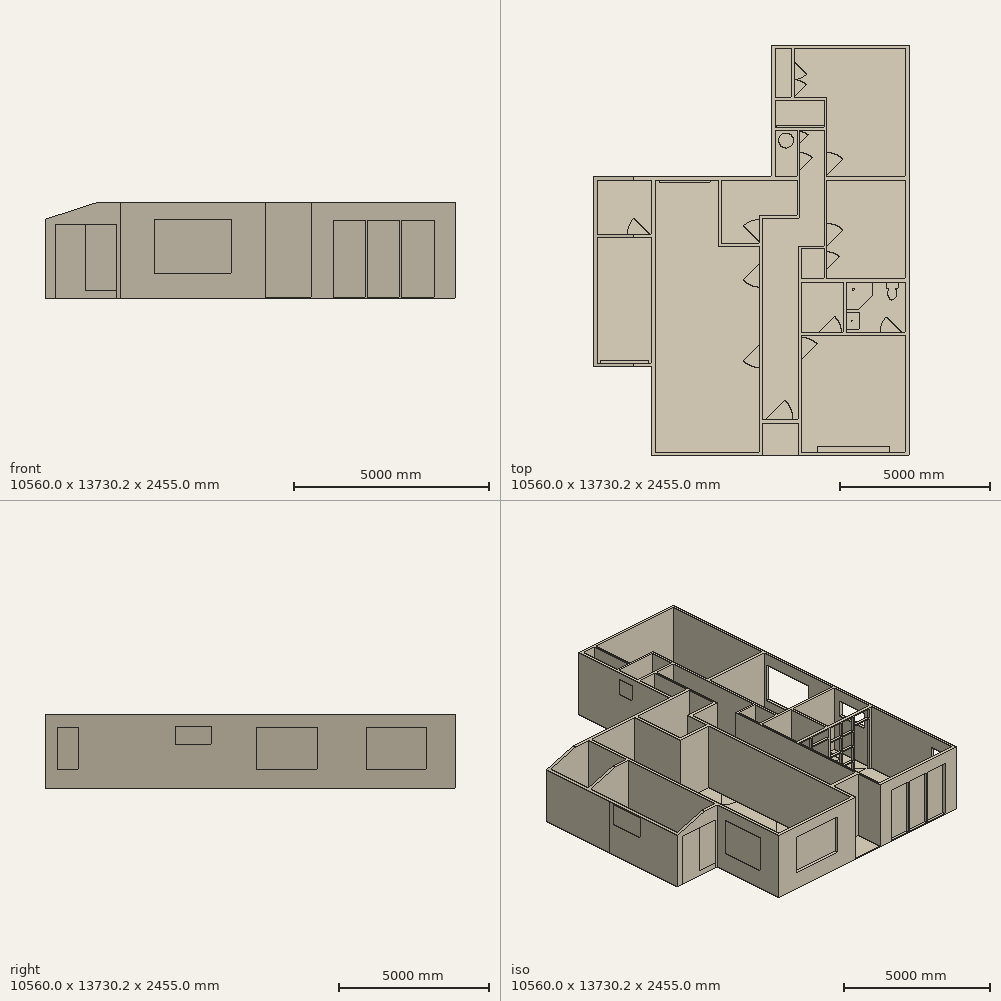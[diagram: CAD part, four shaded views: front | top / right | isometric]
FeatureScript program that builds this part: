
annotation { "Feature Type Name" : "Feature", "Feature Type Description" : "" }
export const myFeature = defineFeature(function(context is Context, id is Id, definition is map)
    precondition{}
    {
        {
            var Q0;
            Q0=qCreatedBy(makeId("Top.planeOp"),FACE);
            var sketch = newSketch(context, id + "F0", { "sketchPlane" : qUnion([Q0])});
            skLineSegment(sketch, "E0.bottom", {"start": v(0, 0) * mm, "end": v(3730, 0) * mm});
            skLineSegment(sketch, "E0.left", {"start": v(0, 0) * mm, "end": v(0, 2970) * mm});
            skLineSegment(sketch, "E0.right", {"start": v(3730, 0) * mm, "end": v(3730, 1060) * mm});
            skLineSegment(sketch, "E1.bottom", {"start": v(115, 115) * mm, "end": v(3615, 115) * mm});
            skLineSegment(sketch, "E2.bottom", {"start": v(3730, 1060) * mm, "end": v(4920, 1060) * mm});
            skLineSegment(sketch, "E2.right", {"start": v(4920, 1210) * mm, "end": v(4920, 7010) * mm});
            skLineSegment(sketch, "E3", {"start": v(3730, 1210) * mm, "end": v(4920, 1210) * mm});
            skLineSegment(sketch, "E4.bottom", {"start": v(5010, 5920) * mm, "end": v(5780, 5920) * mm});
            skLineSegment(sketch, "E4.top", {"start": v(4920, 0) * mm, "end": v(8625, 0) * mm});
            skLineSegment(sketch, "E4.left", {"start": v(4920, 5920) * mm, "end": v(4920, 1210) * mm});
            skLineSegment(sketch, "E4.right", {"start": v(8625, 5920) * mm, "end": v(8625, 0) * mm});
            skLineSegment(sketch, "E5.bottom", {"start": v(8510, 115) * mm, "end": v(5010, 115) * mm});
            skLineSegment(sketch, "E5.top", {"start": v(8510, 5805) * mm, "end": v(6510, 5805) * mm});
            skLineSegment(sketch, "E5.left", {"start": v(8510, 115) * mm, "end": v(8510, 4105) * mm});
            skLineSegment(sketch, "E5.right", {"start": v(5010, 115) * mm, "end": v(5010, 4105) * mm});
            skLineSegment(sketch, "E6", {"start": v(5780, 5920) * mm, "end": v(5780, 6920) * mm});
            skLineSegment(sketch, "E7", {"start": v(8625, 5920) * mm, "end": v(8625, 9335) * mm});
            skLineSegment(sketch, "E8", {"start": v(8510, 9335) * mm, "end": v(5870, 9335) * mm});
            skLineSegment(sketch, "E9.top", {"start": v(5870, 9220) * mm, "end": v(8510, 9220) * mm});
            skLineSegment(sketch, "E9.left", {"start": v(5870, 5920) * mm, "end": v(5870, 9220) * mm});
            skLineSegment(sketch, "E9.right", {"start": v(8510, 5920) * mm, "end": v(8510, 9220) * mm});
            skLineSegment(sketch, "E10.trimOffspring", {"start": v(5870, 5920) * mm, "end": v(8510, 5920) * mm});
            skLineSegment(sketch, "E11", {"start": v(5780, 7010) * mm, "end": v(4920, 7010) * mm});
            skLineSegment(sketch, "E12", {"start": v(5010, 5920) * mm, "end": v(5010, 6920) * mm});
            skLineSegment(sketch, "E13", {"start": v(5010, 6920) * mm, "end": v(5780, 6920) * mm});
            skLineSegment(sketch, "E14", {"start": v(3615, 7000) * mm, "end": v(2235, 7000) * mm});
            skLineSegment(sketch, "E15", {"start": v(2235, 7000) * mm, "end": v(2235, 9220) * mm});
            skLineSegment(sketch, "E16", {"start": v(2235, 9335) * mm, "end": v(4025, 9335) * mm});
            skLineSegment(sketch, "E17", {"start": v(4025, 9335) * mm, "end": v(4025, 13730) * mm});
            skLineSegment(sketch, "E18", {"start": v(4025, 13730) * mm, "end": v(8625, 13730) * mm});
            skLineSegment(sketch, "E19", {"start": v(8625, 9335) * mm, "end": v(8625, 13730) * mm});
            skLineSegment(sketch, "E20", {"start": v(5780, 9335) * mm, "end": v(5780, 10895) * mm});
            skLineSegment(sketch, "E21", {"start": v(5780, 11895) * mm, "end": v(4140, 11895) * mm});
            skLineSegment(sketch, "E22", {"start": v(5870, 9335) * mm, "end": v(5870, 11985) * mm});
            skLineSegment(sketch, "E23", {"start": v(5870, 11985) * mm, "end": v(4770, 11985) * mm});
            skLineSegment(sketch, "E24", {"start": v(4140, 11985) * mm, "end": v(4140, 13615) * mm});
            skLineSegment(sketch, "E25", {"start": v(4140, 13615) * mm, "end": v(4680, 13615) * mm});
            skLineSegment(sketch, "E26", {"start": v(8510, 13615) * mm, "end": v(8510, 9335) * mm});
            skLineSegment(sketch, "E27", {"start": v(4140, 9335) * mm, "end": v(4870, 9335) * mm});
            skLineSegment(sketch, "E28", {"start": v(3615, 7115) * mm, "end": v(2350, 7115) * mm});
            skLineSegment(sketch, "E29", {"start": v(2350, 7115) * mm, "end": v(2350, 9220) * mm});
            skLineSegment(sketch, "E30", {"start": v(2350, 9220) * mm, "end": v(4870, 9220) * mm});
            skLineSegment(sketch, "E31", {"start": v(4870, 9220) * mm, "end": v(4870, 8040) * mm});
            skLineSegment(sketch, "E32", {"start": v(4870, 8040) * mm, "end": v(3615, 8040) * mm});
            skLineSegment(sketch, "E33", {"start": v(4960, 7925) * mm, "end": v(4960, 9335) * mm});
            skLineSegment(sketch, "E34", {"start": v(4140, 11895) * mm, "end": v(4140, 10985) * mm});
            skLineSegment(sketch, "E35", {"start": v(4140, 10895) * mm, "end": v(5780, 10895) * mm});
            skLineSegment(sketch, "E36.trimOffspring", {"start": v(4140, 10895) * mm, "end": v(4140, 9335) * mm});
            skLineSegment(sketch, "E37.trimOffspring", {"start": v(5780, 10985) * mm, "end": v(5780, 11895) * mm});
            skLineSegment(sketch, "E38", {"start": v(4770, 13615) * mm, "end": v(4770, 11985) * mm});
            skLineSegment(sketch, "E39", {"start": v(4680, 13615) * mm, "end": v(4680, 11985) * mm});
            skLineSegment(sketch, "E40.trimOffspring", {"start": v(4770, 13615) * mm, "end": v(8510, 13615) * mm});
            skLineSegment(sketch, "E41.trimOffspring", {"start": v(4680, 11985) * mm, "end": v(4140, 11985) * mm});
            skLineSegment(sketch, "E42", {"start": v(2235, 9335) * mm, "end": v(-1935, 9335) * mm});
            skLineSegment(sketch, "E43", {"start": v(-1935, 9335) * mm, "end": v(-1935, 7285) * mm});
            skLineSegment(sketch, "E44", {"start": v(-1820, 7285) * mm, "end": v(0, 7285) * mm});
            skLineSegment(sketch, "E45", {"start": v(0, 9220) * mm, "end": v(-1820, 9220) * mm});
            skLineSegment(sketch, "E46", {"start": v(-1820, 9220) * mm, "end": v(-1820, 7400) * mm});
            skLineSegment(sketch, "E47", {"start": v(-1820, 7400) * mm, "end": v(0, 7400) * mm});
            skLineSegment(sketch, "E48", {"start": v(0, 9220) * mm, "end": v(0, 7400) * mm});
            skLineSegment(sketch, "E49", {"start": v(115, 9220) * mm, "end": v(2235, 9220) * mm});
            skLineSegment(sketch, "E50", {"start": v(4960, 9335) * mm, "end": v(4960, 10895) * mm});
            skLineSegment(sketch, "E51", {"start": v(4870, 10895) * mm, "end": v(4870, 9335) * mm});
            skLineSegment(sketch, "E52", {"start": v(115, 9220) * mm, "end": v(115, 115) * mm});
            skLineSegment(sketch, "E53", {"start": v(-1935, 7285) * mm, "end": v(-1935, 2970) * mm});
            skLineSegment(sketch, "E54", {"start": v(-1935, 2970) * mm, "end": v(0, 2970) * mm});
            skLineSegment(sketch, "E55", {"start": v(-1820, 7285) * mm, "end": v(-1820, 3085) * mm});
            skLineSegment(sketch, "E56", {"start": v(-1820, 3085) * mm, "end": v(0, 3085) * mm});
            skPoint(sketch, "E57", {"position": v(4960, 10895) * mm});
            skLineSegment(sketch, "E58", {"start": v(4140, 10985) * mm, "end": v(5780, 10985) * mm});
            skLineSegment(sketch, "E59", {"start": v(3615, 7115) * mm, "end": v(3615, 8040) * mm});
            skLineSegment(sketch, "E60.trimOffspring", {"start": v(0, 7285) * mm, "end": v(0, 3085) * mm});
            skLineSegment(sketch, "E61.trimOffspring", {"start": v(3730, 7925) * mm, "end": v(4960, 7925) * mm});
            skLineSegment(sketch, "E62.trimOffspring", {"start": v(4920, 1060) * mm, "end": v(4920, 0) * mm});
            skLineSegment(sketch, "E63.trimOffspring", {"start": v(5780, 7010) * mm, "end": v(5780, 9335) * mm});
            skLineSegment(sketch, "E64", {"start": v(6510, 4105) * mm, "end": v(6510, 5805) * mm});
            skLineSegment(sketch, "E65", {"start": v(6410, 4105) * mm, "end": v(6410, 5805) * mm});
            skLineSegment(sketch, "E66", {"start": v(3730, 7925) * mm, "end": v(3730, 1210) * mm});
            skLineSegment(sketch, "E67", {"start": v(3615, 7000) * mm, "end": v(3615, 115) * mm});
            skLineSegment(sketch, "E68.trimOffspring", {"start": v(6410, 5805) * mm, "end": v(5010, 5805) * mm});
            skLineSegment(sketch, "E69.trimOffspring", {"start": v(8510, 4105) * mm, "end": v(8510, 5805) * mm});
            skLineSegment(sketch, "E70.trimOffspring", {"start": v(5010, 4105) * mm, "end": v(5010, 5805) * mm});
            skLineSegment(sketch, "E71", {"start": v(6410, 4105) * mm, "end": v(6510, 4105) * mm});
            skSolve(sketch);
        }
        {
            var Q0;
            Q0=makeQuery(id+"F0.imprint","IMPRINT",FACE,{"disambiguationData":[TD([[makeQuery(id+"F0.imprint","IMPRINT",EDGE,{"derivedFrom":sQuery(id+"F0.wireOp",EDGE,"E0.bottom")}),1.0]])]});
            var Q1;
            {var subQ0=sQuery(id+"F0.wireOp",EDGE,"E2.bottom");Q1=makeQuery(id+"F0.imprint","IMPRINT",FACE,{"disambiguationData":[TD([[makeQuery(id+"F0.imprint","IMPRINT",EDGE,{"derivedFrom":subQ0}),1.0]])]});}
            var Q2;
            {var subQ3=sQuery(id+"F0.wireOp",EDGE,"E4.bottom");Q2=makeQuery(id+"F0.imprint","IMPRINT",FACE,{"disambiguationData":[TD([[makeQuery(id+"F0.imprint","IMPRINT",EDGE,{"derivedFrom":subQ3}),-1.0]])]});}
            extrude(context, id + "F1", {"entities" : qUnion([Q0, Q1, Q2]), "depth" : 2430 * mm});
        }
        {
            var Q0;
            Q0=qCreatedBy(makeId("Front.planeOp"),FACE);
            var sketch = newSketch(context, id + "F2", { "sketchPlane" : qUnion([Q0])});
            skLineSegment(sketch, "E72", {"start": v(0, 0) * mm, "end": v(0, 2430) * mm});
            skLineSegment(sketch, "E73", {"start": v(0, 2430) * mm, "end": v(-1935, 1850) * mm, "construction": true});
            skLineSegment(sketch, "E74", {"start": v(-1935, 1850) * mm, "end": v(-1935, 3117.7) * mm});
            skLineSegment(sketch, "E75", {"start": v(-1935, 3117.7) * mm, "end": v(0, 3117.7) * mm});
            skLineSegment(sketch, "E76", {"start": v(0, 3117.7) * mm, "end": v(0, 2430) * mm});
            skLineSegment(sketch, "E77", {"start": v(-1935, 2005) * mm, "end": v(0, 2630) * mm});
            skSolve(sketch);
        }
        {
            var Q0;
            Q0=qSketchRegion(id+"F2",true);
            extrude(context, id + "F3", {"entities" : qUnion([Q0]), "operationType" : NewBodyOperationType.REMOVE, "endBound" : BoundingType.THROUGH_ALL, "oppositeDirection" : true, "depth" : 25 * mm});
        }
        {
            var Q0;
            Q0=qCreatedBy(makeId("Top.planeOp"),FACE);
            var sketch = newSketch(context, id + "F4", { "sketchPlane" : qUnion([Q0])});
            skLineSegment(sketch, "E78", {"start": v(0, 0) * mm, "end": v(8625, 0) * mm});
            skLineSegment(sketch, "E79", {"start": v(8625, 0) * mm, "end": v(8625, 13730) * mm});
            skLineSegment(sketch, "E80", {"start": v(8625, 13730) * mm, "end": v(4025, 13730) * mm});
            skLineSegment(sketch, "E81", {"start": v(4025, 13730) * mm, "end": v(4025, 9335) * mm});
            skLineSegment(sketch, "E82", {"start": v(4025, 9335) * mm, "end": v(-1935, 9335) * mm});
            skLineSegment(sketch, "E83", {"start": v(-1935, 9335) * mm, "end": v(-1935, 2970) * mm});
            skLineSegment(sketch, "E84", {"start": v(-1935, 2970) * mm, "end": v(0, 2970) * mm});
            skLineSegment(sketch, "E85", {"start": v(0, 2970) * mm, "end": v(0, 0) * mm});
            skSolve(sketch);
        }
        {
            var Q0;
            Q0=qSketchRegion(id+"F4",true);
            extrude(context, id + "F5", {"entities" : qUnion([Q0]), "operationType" : NewBodyOperationType.ADD, "oppositeDirection" : true, "depth" : 25 * mm});
        }
        {
            var Q0;
            Q0=makeQuery(id+"F1.opExtrude","SWEPT_FACE",FACE,{"disambiguationData":[OSD([sQuery(id+"F0.wireOp",EDGE,"E71")])]});
            var sketch = newSketch(context, id + "F6", { "sketchPlane" : qUnion([Q0])});
            skLineSegment(sketch, "E86", {"start": v(6410, 0) * mm, "end": v(6410, 1980) * mm});
            skLineSegment(sketch, "E87", {"start": v(6410, 2430) * mm, "end": v(6510, 2430) * mm});
            skLineSegment(sketch, "E88", {"start": v(6510, 2385) * mm, "end": v(6510, 1833.75) * mm});
            skLineSegment(sketch, "E89", {"start": v(6510, 0) * mm, "end": v(6410, 0) * mm});
            skLineSegment(sketch, "E90", {"start": v(6410, 2430) * mm, "end": v(5010, 2430) * mm});
            skLineSegment(sketch, "E91", {"start": v(5010, 2430) * mm, "end": v(5010, 0) * mm});
            skLineSegment(sketch, "E92", {"start": v(5010, 0) * mm, "end": v(5650, 0) * mm});
            skLineSegment(sketch, "E93", {"start": v(6510, 2430) * mm, "end": v(8510, 2430) * mm});
            skLineSegment(sketch, "E94", {"start": v(8510, 2430) * mm, "end": v(8510, 0) * mm});
            skLineSegment(sketch, "E95", {"start": v(8510, 0) * mm, "end": v(8420, 0) * mm});
            skLineSegment(sketch, "E96", {"start": v(5055, 45) * mm, "end": v(5055, 596.25) * mm});
            skLineSegment(sketch, "E97", {"start": v(5055, 2385) * mm, "end": v(5605, 2385) * mm});
            skLineSegment(sketch, "E98", {"start": v(5055, 45) * mm, "end": v(5605, 45) * mm});
            skLineSegment(sketch, "E99", {"start": v(5605, 45) * mm, "end": v(5605, 596.25) * mm});
            skLineSegment(sketch, "E100", {"start": v(5650, 0) * mm, "end": v(5650, 1980) * mm});
            skLineSegment(sketch, "E101", {"start": v(5650, 1980) * mm, "end": v(6410, 1980) * mm});
            skLineSegment(sketch, "E102", {"start": v(6410, 1980) * mm, "end": v(6410, 0) * mm});
            skLineSegment(sketch, "E103", {"start": v(5650, 2025) * mm, "end": v(5650, 2385) * mm});
            skLineSegment(sketch, "E104", {"start": v(5650, 2025) * mm, "end": v(6410, 2025) * mm});
            skLineSegment(sketch, "E105", {"start": v(7660, 0) * mm, "end": v(7660, 1980) * mm});
            skLineSegment(sketch, "E106", {"start": v(7660, 1980) * mm, "end": v(8420, 1980) * mm});
            skLineSegment(sketch, "E107", {"start": v(8420, 1980) * mm, "end": v(8420, 0) * mm});
            skLineSegment(sketch, "E108", {"start": v(6510, 2385) * mm, "end": v(7062.5, 2385) * mm});
            skLineSegment(sketch, "E109", {"start": v(8420, 2025) * mm, "end": v(7660, 2025) * mm});
            skLineSegment(sketch, "E110", {"start": v(7615, 2025) * mm, "end": v(7615, 1833.75) * mm});
            skLineSegment(sketch, "E111", {"start": v(8420, 2385) * mm, "end": v(8420, 2025) * mm});
            skLineSegment(sketch, "E112", {"start": v(7615, 2025) * mm, "end": v(7615, 2385) * mm});
            skLineSegment(sketch, "E113", {"start": v(7660, 2025) * mm, "end": v(7660, 2385) * mm});
            skLineSegment(sketch, "E114", {"start": v(6510, 45) * mm, "end": v(7062.5, 45) * mm});
            skLineSegment(sketch, "E115", {"start": v(6510, 596.25) * mm, "end": v(7062.5, 596.25) * mm});
            skLineSegment(sketch, "E116", {"start": v(6510, 641.25) * mm, "end": v(7062.5, 641.25) * mm});
            skLineSegment(sketch, "E117", {"start": v(7615, 1192.5) * mm, "end": v(7107.5, 1192.5) * mm});
            skLineSegment(sketch, "E118", {"start": v(6510, 1237.5) * mm, "end": v(7062.5, 1237.5) * mm});
            skLineSegment(sketch, "E119", {"start": v(6510, 1788.75) * mm, "end": v(7062.5, 1788.75) * mm});
            skLineSegment(sketch, "E120", {"start": v(6510, 1833.75) * mm, "end": v(7062.5, 1833.75) * mm});
            skLineSegment(sketch, "E121", {"start": v(5605, 596.25) * mm, "end": v(5055, 596.25) * mm});
            skLineSegment(sketch, "E122", {"start": v(5055, 641.25) * mm, "end": v(5605, 641.25) * mm});
            skLineSegment(sketch, "E123", {"start": v(5605, 1192.5) * mm, "end": v(5055, 1192.5) * mm});
            skLineSegment(sketch, "E124", {"start": v(5055, 1237.5) * mm, "end": v(5605, 1237.5) * mm});
            skLineSegment(sketch, "E125", {"start": v(5605, 1788.75) * mm, "end": v(5055, 1788.75) * mm});
            skLineSegment(sketch, "E126", {"start": v(5055, 1833.75) * mm, "end": v(5605, 1833.75) * mm});
            skLineSegment(sketch, "E127", {"start": v(5207.26, 2385) * mm, "end": v(5207.26, 1833.75) * mm, "construction": true});
            skLineSegment(sketch, "E128", {"start": v(5202.38, 1788.75) * mm, "end": v(5202.38, 1237.5) * mm, "construction": true});
            skLineSegment(sketch, "E129", {"start": v(5202.38, 1192.5) * mm, "end": v(5202.38, 641.25) * mm, "construction": true});
            skLineSegment(sketch, "E130", {"start": v(5196.62, 596.25) * mm, "end": v(5196.62, 45) * mm, "construction": true});
            skLineSegment(sketch, "E131", {"start": v(6622.85, 45) * mm, "end": v(6622.85, 596.25) * mm, "construction": true});
            skLineSegment(sketch, "E132", {"start": v(6622.85, 641.25) * mm, "end": v(6622.85, 1192.5) * mm, "construction": true});
            skLineSegment(sketch, "E133", {"start": v(6616.16, 1788.75) * mm, "end": v(6616.16, 1237.5) * mm, "construction": true});
            skLineSegment(sketch, "E134", {"start": v(6631.24, 2385) * mm, "end": v(6631.24, 1833.75) * mm, "construction": true});
            skLineSegment(sketch, "E135.trimOffspring", {"start": v(7660, 2385) * mm, "end": v(8420, 2385) * mm});
            skLineSegment(sketch, "E136.trimOffspring", {"start": v(6510, 1788.75) * mm, "end": v(6510, 1237.5) * mm});
            skLineSegment(sketch, "E137.trimOffspring", {"start": v(6410, 2025) * mm, "end": v(6410, 2385) * mm});
            skLineSegment(sketch, "E138.trimOffspring", {"start": v(7615, 1788.75) * mm, "end": v(7615, 1237.5) * mm});
            skLineSegment(sketch, "E139.trimOffspring", {"start": v(7615, 1192.5) * mm, "end": v(7615, 641.25) * mm});
            skLineSegment(sketch, "E140.trimOffspring", {"start": v(6510, 1192.5) * mm, "end": v(6510, 641.25) * mm});
            skLineSegment(sketch, "E141.trimOffspring", {"start": v(6510, 596.25) * mm, "end": v(6510, 45) * mm});
            skLineSegment(sketch, "E142.trimOffspring", {"start": v(7615, 596.25) * mm, "end": v(7615, 45) * mm});
            skPoint(sketch, "E143.orphan", {"position": v(7615, 0) * mm});
            skLineSegment(sketch, "E144.trimOffspring", {"start": v(5605, 641.25) * mm, "end": v(5605, 1192.5) * mm});
            skLineSegment(sketch, "E145.trimOffspring", {"start": v(5055, 641.25) * mm, "end": v(5055, 1192.5) * mm});
            skLineSegment(sketch, "E146.trimOffspring", {"start": v(5055, 1237.5) * mm, "end": v(5055, 1788.75) * mm});
            skLineSegment(sketch, "E147.trimOffspring", {"start": v(5605, 1237.5) * mm, "end": v(5605, 1788.75) * mm});
            skLineSegment(sketch, "E148.trimOffspring", {"start": v(5055, 1833.75) * mm, "end": v(5055, 2385) * mm});
            skLineSegment(sketch, "E149.trimOffspring", {"start": v(5605, 1833.75) * mm, "end": v(5605, 2385) * mm});
            skLineSegment(sketch, "E150.trimOffspring", {"start": v(5650, 2385) * mm, "end": v(6410, 2385) * mm});
            skLineSegment(sketch, "E151.trimOffspring", {"start": v(7660, 0) * mm, "end": v(6510, 0) * mm});
            skLineSegment(sketch, "E152", {"start": v(7062.5, 2385) * mm, "end": v(7062.5, 1833.75) * mm});
            skLineSegment(sketch, "E153", {"start": v(7107.5, 2385) * mm, "end": v(7107.5, 1833.75) * mm});
            skLineSegment(sketch, "E154.trimOffspring", {"start": v(7062.5, 1192.5) * mm, "end": v(6510, 1192.5) * mm});
            skLineSegment(sketch, "E155.trimOffspring", {"start": v(7107.5, 1237.5) * mm, "end": v(7615, 1237.5) * mm});
            skLineSegment(sketch, "E156.trimOffspring", {"start": v(7107.5, 1833.75) * mm, "end": v(7615, 1833.75) * mm});
            skLineSegment(sketch, "E157.trimOffspring", {"start": v(7107.5, 1788.75) * mm, "end": v(7615, 1788.75) * mm});
            skLineSegment(sketch, "E158.trimOffspring", {"start": v(7107.5, 2385) * mm, "end": v(7615, 2385) * mm});
            skLineSegment(sketch, "E159.trimOffspring", {"start": v(7107.5, 596.25) * mm, "end": v(7615, 596.25) * mm});
            skLineSegment(sketch, "E160.trimOffspring", {"start": v(7107.5, 641.25) * mm, "end": v(7615, 641.25) * mm});
            skLineSegment(sketch, "E161.trimOffspring", {"start": v(7107.5, 45) * mm, "end": v(7615, 45) * mm});
            skLineSegment(sketch, "E162.trimOffspring", {"start": v(7062.5, 596.25) * mm, "end": v(7062.5, 45) * mm});
            skLineSegment(sketch, "E163.trimOffspring", {"start": v(7107.5, 596.25) * mm, "end": v(7107.5, 45) * mm});
            skLineSegment(sketch, "E164.trimOffspring", {"start": v(7107.5, 1192.5) * mm, "end": v(7107.5, 641.25) * mm});
            skLineSegment(sketch, "E165.trimOffspring", {"start": v(7062.5, 1192.5) * mm, "end": v(7062.5, 641.25) * mm});
            skLineSegment(sketch, "E166.trimOffspring", {"start": v(7062.5, 1788.75) * mm, "end": v(7062.5, 1237.5) * mm});
            skLineSegment(sketch, "E167.trimOffspring", {"start": v(7107.5, 1788.75) * mm, "end": v(7107.5, 1237.5) * mm});
            skSolve(sketch);
        }
        {
            var Q0;
            {var subQ0=sQuery(id+"F6.wireOp",EDGE,"E105");Q0=makeQuery(id+"F6.imprint","IMPRINT",FACE,{"disambiguationData":[TD([[makeQuery(id+"F6.imprint","IMPRINT",EDGE,{"derivedFrom":subQ0}),-1.0]])]});}
            var Q1;
            {var subQ2=sQuery(id+"F6.wireOp",EDGE,"E100");Q1=makeQuery(id+"F6.imprint","IMPRINT",FACE,{"disambiguationData":[TD([[makeQuery(id+"F6.imprint","IMPRINT",EDGE,{"derivedFrom":subQ2}),-1.0]])]});}
            var Q2;
            {var subQ5=sQuery(id+"F6.wireOp",EDGE,"E90");Q2=makeQuery(id+"F6.imprint","IMPRINT",FACE,{"disambiguationData":[TD([[makeQuery(id+"F6.imprint","IMPRINT",EDGE,{"derivedFrom":subQ5}),1.0]])]});}
            var Q3;
            {var subQ14=sQuery(id+"F6.wireOp",EDGE,"E93");Q3=makeQuery(id+"F6.imprint","IMPRINT",FACE,{"disambiguationData":[TD([[makeQuery(id+"F6.imprint","IMPRINT",EDGE,{"derivedFrom":subQ14}),-1.0]])]});}
            var Q4;
            {var subQ5=sQuery(id+"F6.wireOp",EDGE,"E87");Q4=makeQuery(id+"F6.imprint","IMPRINT",FACE,{"disambiguationData":[TD([[makeQuery(id+"F6.imprint","IMPRINT",EDGE,{"derivedFrom":subQ5}),-1.0]])]});}
            extrude(context, id + "F7", {"entities" : qUnion([Q0, Q1, Q2, Q3, Q4]), "operationType" : NewBodyOperationType.ADD, "depth" : 100 * mm});
        }
        {
            var Q0;
            Q0=makeQuery(id+"F1.opExtrude","SWEPT_FACE",FACE,{"disambiguationData":[OSD([sQuery(id+"F0.wireOp",EDGE,"E5.left")])]});
            var sketch = newSketch(context, id + "F8", { "sketchPlane" : qUnion([Q0])});
            skLineSegment(sketch, "E168.bottom", {"start": v(-1115, 600) * mm, "end": v(-415, 600) * mm});
            skLineSegment(sketch, "E168.top", {"start": v(-1115, 2000) * mm, "end": v(-415, 2000) * mm});
            skLineSegment(sketch, "E168.left", {"start": v(-1115, 600) * mm, "end": v(-1115, 2000) * mm});
            skLineSegment(sketch, "E168.right", {"start": v(-415, 600) * mm, "end": v(-415, 2000) * mm});
            skLineSegment(sketch, "E169.bottom", {"start": v(-4355, 2030) * mm, "end": v(-5555, 2030) * mm});
            skLineSegment(sketch, "E169.top", {"start": v(-4355, 1430) * mm, "end": v(-5555, 1430) * mm});
            skLineSegment(sketch, "E169.left", {"start": v(-4355, 2030) * mm, "end": v(-4355, 1430) * mm});
            skLineSegment(sketch, "E169.right", {"start": v(-5555, 2030) * mm, "end": v(-5555, 1430) * mm});
            skLineSegment(sketch, "E170.bottom", {"start": v(-7070, 2000) * mm, "end": v(-9120, 2000) * mm});
            skLineSegment(sketch, "E170.top", {"start": v(-7070, 600) * mm, "end": v(-9120, 600) * mm});
            skLineSegment(sketch, "E170.left", {"start": v(-7070, 2000) * mm, "end": v(-7070, 600) * mm});
            skLineSegment(sketch, "E170.right", {"start": v(-9120, 2000) * mm, "end": v(-9120, 600) * mm});
            skLineSegment(sketch, "E171.bottom", {"start": v(-10735, 2000) * mm, "end": v(-12765, 2000) * mm});
            skLineSegment(sketch, "E171.top", {"start": v(-10735, 600) * mm, "end": v(-12765, 600) * mm});
            skLineSegment(sketch, "E171.left", {"start": v(-10735, 2000) * mm, "end": v(-10735, 600) * mm});
            skLineSegment(sketch, "E171.right", {"start": v(-12765, 2000) * mm, "end": v(-12765, 600) * mm});
            skSolve(sketch);
        }
        {
            var Q0;
            Q0 = qSketchRegion(id + "F8", true);
            extrude(context, id + "F9", {"entities" : qUnion([Q0]), "operationType" : NewBodyOperationType.REMOVE, "endBound" : BoundingType.UP_TO_NEXT, "oppositeDirection" : true, "depth" : 25 * mm});
        }
        {
            var Q0;
            Q0=makeQuery(id+"F5.boolean.opBoolean","MERGE",FACE,{"derivedFrom":[makeQuery(id+"F1.opExtrude","SWEPT_FACE",FACE,{"disambiguationData":[OSD([sQuery(id+"F0.wireOp",EDGE,"E0.bottom")])]}),makeQuery(id+"F1.opExtrude","SWEPT_FACE",FACE,{"disambiguationData":[OSD([sQuery(id+"F0.wireOp",EDGE,"E4.top")])]}),makeQuery(id+"F5.opExtrude","SWEPT_FACE",FACE,{"disambiguationData":[OSD([sQuery(id+"F4.wireOp",EDGE,"E78")])]})]});
            var sketch = newSketch(context, id + "F10", { "sketchPlane" : qUnion([Q0])});
            skLineSegment(sketch, "E172", {"start": v(4920, 0) * mm, "end": v(8625, 0) * mm, "construction": true});
            skLineSegment(sketch, "E173.bottom", {"start": v(5470, 0) * mm, "end": v(6311.67, 0) * mm});
            skLineSegment(sketch, "E173.top", {"start": v(5470, 1980) * mm, "end": v(6311.67, 1980) * mm});
            skLineSegment(sketch, "E173.left", {"start": v(5470, 0) * mm, "end": v(5470, 1980) * mm});
            skLineSegment(sketch, "E173.right", {"start": v(6311.67, 0) * mm, "end": v(6311.67, 1980) * mm});
            skLineSegment(sketch, "E174.bottom", {"start": v(6351.67, 0) * mm, "end": v(7193.33, 0) * mm});
            skLineSegment(sketch, "E174.top", {"start": v(6351.67, 1980) * mm, "end": v(7193.33, 1980) * mm});
            skLineSegment(sketch, "E174.left", {"start": v(6351.67, 0) * mm, "end": v(6351.67, 1980) * mm});
            skLineSegment(sketch, "E174.right", {"start": v(7193.33, 0) * mm, "end": v(7193.33, 1980) * mm});
            skLineSegment(sketch, "E175.bottom", {"start": v(7233.33, 0) * mm, "end": v(8075, 0) * mm});
            skLineSegment(sketch, "E175.top", {"start": v(7233.33, 1980) * mm, "end": v(8075, 1980) * mm});
            skLineSegment(sketch, "E175.left", {"start": v(7233.33, 0) * mm, "end": v(7233.33, 1980) * mm});
            skLineSegment(sketch, "E175.right", {"start": v(8075, 0) * mm, "end": v(8075, 1980) * mm});
            skLineSegment(sketch, "E176", {"start": v(6311.67, 1980) * mm, "end": v(6351.67, 1980) * mm, "construction": true});
            skLineSegment(sketch, "E177", {"start": v(7193.33, 1980) * mm, "end": v(7233.33, 1980) * mm, "construction": true});
            skLineSegment(sketch, "E178", {"start": v(3730, 0) * mm, "end": v(0, 0) * mm, "construction": true});
            skLineSegment(sketch, "E179.bottom", {"start": v(865, 2000) * mm, "end": v(2865, 2000) * mm});
            skLineSegment(sketch, "E179.top", {"start": v(865, 600) * mm, "end": v(2865, 600) * mm});
            skLineSegment(sketch, "E179.left", {"start": v(865, 2000) * mm, "end": v(865, 600) * mm});
            skLineSegment(sketch, "E179.right", {"start": v(2865, 2000) * mm, "end": v(2865, 600) * mm});
            skSolve(sketch);
        }
        {
            var Q0;
            Q0 = qSketchRegion(id + "F10", true);
            extrude(context, id + "F11", {"entities" : qUnion([Q0]), "operationType" : NewBodyOperationType.REMOVE, "oppositeDirection" : true, "depth" : 120 * mm});
        }
        {
            var Q0;
            Q0=makeQuery(id+"F1.opExtrude","SWEPT_FACE",FACE,{"disambiguationData":[OSD([sQuery(id+"F0.wireOp",EDGE,"E5.bottom")])]});
            var sketch = newSketch(context, id + "F12", { "sketchPlane" : qUnion([Q0])});
            skLineSegment(sketch, "E180.bottom", {"start": v(-8075, 1980) * mm, "end": v(-5470, 1980) * mm});
            skLineSegment(sketch, "E180.top", {"start": v(-8075, 0) * mm, "end": v(-5470, 0) * mm});
            skLineSegment(sketch, "E180.left", {"start": v(-8075, 1980) * mm, "end": v(-8075, 0) * mm});
            skLineSegment(sketch, "E180.right", {"start": v(-5470, 1980) * mm, "end": v(-5470, 0) * mm});
            skLineSegment(sketch, "E181.bottom", {"start": v(-2897.25, 2043.33) * mm, "end": v(-835.08, 2043.33) * mm});
            skLineSegment(sketch, "E181.top", {"start": v(-2897.25, 579.48) * mm, "end": v(-835.08, 579.48) * mm});
            skLineSegment(sketch, "E181.left", {"start": v(-2897.25, 2043.33) * mm, "end": v(-2897.25, 579.48) * mm});
            skLineSegment(sketch, "E181.right", {"start": v(-835.08, 2043.33) * mm, "end": v(-835.08, 579.48) * mm});
            skSolve(sketch);
        }
        {
            var Q0;
            Q0 = qSketchRegion(id + "F12", true);
            extrude(context, id + "F13", {"entities" : qUnion([Q0]), "operationType" : NewBodyOperationType.ADD, "oppositeDirection" : true, "depth" : 5 * mm});
        }
        {
            var Q0;
            Q0=makeQuery(id+"F1.opExtrude","SWEPT_FACE",FACE,{"disambiguationData":[OSD([sQuery(id+"F0.wireOp",EDGE,"E26")])]});
            var sketch = newSketch(context, id + "F14", { "sketchPlane" : qUnion([Q0])});
            skLineSegment(sketch, "E182.bottom", {"start": v(-12765, 2000) * mm, "end": v(-10735, 2000) * mm});
            skLineSegment(sketch, "E182.top", {"start": v(-12765, 600) * mm, "end": v(-10735, 600) * mm});
            skLineSegment(sketch, "E182.left", {"start": v(-12765, 2000) * mm, "end": v(-12765, 600) * mm});
            skLineSegment(sketch, "E182.right", {"start": v(-10735, 2000) * mm, "end": v(-10735, 600) * mm});
            skSolve(sketch);
        }
        {
            var Q0;
            Q0 = qSketchRegion(id + "F14", true);
            extrude(context, id + "F15", {"entities" : qUnion([Q0]), "operationType" : NewBodyOperationType.ADD, "oppositeDirection" : true, "depth" : 5 * mm});
        }
        {
            var Q0;
            Q0=makeQuery(id+"F5.boolean.opBoolean","SPLIT",FACE,{"disambiguationData":[TD([makeQuery(id+"F1.opExtrude","SWEPT_FACE",FACE,{"disambiguationData":[OSD([sQuery(id+"F0.wireOp",EDGE,"E1.bottom")])]})])],"derivedFrom":makeQuery(id+"F5.opExtrude","CAP_FACE",FACE,{"disambiguationData":[OSD([sQuery(id+"F4.wireOp",EDGE,"E78"),sQuery(id+"F4.wireOp",EDGE,"E79"),sQuery(id+"F4.wireOp",EDGE,"E80"),sQuery(id+"F4.wireOp",EDGE,"E81"),sQuery(id+"F4.wireOp",EDGE,"E82"),sQuery(id+"F4.wireOp",EDGE,"E83"),sQuery(id+"F4.wireOp",EDGE,"E84"),sQuery(id+"F4.wireOp",EDGE,"E85")])],"isStart":true})});
            var sketch = newSketch(context, id + "F16", { "sketchPlane" : qUnion([Q0])});
            skLineSegment(sketch, "E183", {"start": v(3615, 3705) * mm, "end": v(3077.6, 3167.6) * mm});
            skArc(sketch, "E184", {"start": v(3077.6, 3167.6) * mm, "mid": v(3324.16, 3002.85) * mm, "end": v(3615, 2945) * mm});
            skLineSegment(sketch, "E185", {"start": v(3615, 6400) * mm, "end": v(3077.6, 5862.6) * mm});
            skLineSegment(sketch, "E186", {"start": v(5870, 7010) * mm, "end": v(6407.4, 7547.4) * mm});
            skLineSegment(sketch, "E187", {"start": v(5870, 6220) * mm, "end": v(6294.26, 6644.26) * mm});
            skLineSegment(sketch, "E188", {"start": v(5870, 9385) * mm, "end": v(6407.4, 9922.4) * mm});
            skLineSegment(sketch, "E189", {"start": v(3615, 7140) * mm, "end": v(3077.6, 7677.4) * mm});
            skLineSegment(sketch, "E190", {"start": v(-50, 7400) * mm, "end": v(-587.4, 7937.4) * mm});
            skLineSegment(sketch, "E191", {"start": v(3830, 1210) * mm, "end": v(4466.4, 1846.4) * mm});
            skLineSegment(sketch, "E192", {"start": v(5010, 3195) * mm, "end": v(5547.4, 3732.4) * mm});
            skLineSegment(sketch, "E193", {"start": v(5560, 315) * mm, "end": v(7960, 315) * mm});
            skLineSegment(sketch, "E194", {"start": v(7960, 315) * mm, "end": v(7960, 115) * mm});
            skLineSegment(sketch, "E195", {"start": v(5560, 315) * mm, "end": v(5560, 115) * mm});
            skLineSegment(sketch, "E196", {"start": v(5560, 115) * mm, "end": v(7960, 115) * mm});
            skLineSegment(sketch, "E197", {"start": v(265, 9135) * mm, "end": v(1985, 9135) * mm});
            skLineSegment(sketch, "E198", {"start": v(1985, 9135) * mm, "end": v(1985, 9335) * mm});
            skLineSegment(sketch, "E199", {"start": v(1985, 9335) * mm, "end": v(265, 9335) * mm});
            skLineSegment(sketch, "E200", {"start": v(265, 9335) * mm, "end": v(265, 9135) * mm});
            skLineSegment(sketch, "E201", {"start": v(4960, 9545) * mm, "end": v(5384.26, 9969.26) * mm});
            skLineSegment(sketch, "E202", {"start": v(4960, 10445) * mm, "end": v(5242.84, 10727.84) * mm});
            skLineSegment(sketch, "E203", {"start": v(4770, 13185) * mm, "end": v(5194.26, 12760.74) * mm});
            skLineSegment(sketch, "E204", {"start": v(4770, 11985) * mm, "end": v(5194.26, 12409.26) * mm});
            skArc(sketch, "E205", {"start": v(4730, 1210) * mm, "mid": v(4661.5, 1554.42) * mm, "end": v(4466.4, 1846.4) * mm});
            skArc(sketch, "E206", {"start": v(5547.4, 3732.4) * mm, "mid": v(5300.84, 3897.15) * mm, "end": v(5010, 3955) * mm});
            skArc(sketch, "E207", {"start": v(6294.26, 6644.26) * mm, "mid": v(6099.61, 6774.33) * mm, "end": v(5870, 6820) * mm});
            skArc(sketch, "E208", {"start": v(6407.4, 9922.4) * mm, "mid": v(6160.84, 10087.15) * mm, "end": v(5870, 10145) * mm});
            skArc(sketch, "E209", {"start": v(3615, 7900) * mm, "mid": v(3324.16, 7842.15) * mm, "end": v(3077.6, 7677.4) * mm});
            skArc(sketch, "E210", {"start": v(3077.6, 5862.6) * mm, "mid": v(3324.16, 5697.85) * mm, "end": v(3615, 5640) * mm});
            skArc(sketch, "E211", {"start": v(-587.4, 7937.4) * mm, "mid": v(-752.15, 7690.84) * mm, "end": v(-810, 7400) * mm});
            skArc(sketch, "E212", {"start": v(5242.84, 10727.84) * mm, "mid": v(5113.07, 10814.55) * mm, "end": v(4960, 10845) * mm});
            skArc(sketch, "E213", {"start": v(5194.26, 12409.26) * mm, "mid": v(4999.61, 12539.33) * mm, "end": v(4770, 12585) * mm});
            skArc(sketch, "E214", {"start": v(4770, 12585) * mm, "mid": v(4999.61, 12630.67) * mm, "end": v(5194.26, 12760.74) * mm});
            skLineSegment(sketch, "E215", {"start": v(3830, 1210) * mm, "end": v(4730, 1210) * mm});
            skLineSegment(sketch, "E216", {"start": v(5010, 3195) * mm, "end": v(5010, 3955) * mm});
            skLineSegment(sketch, "E217", {"start": v(3615, 3705) * mm, "end": v(3615, 2945) * mm});
            skLineSegment(sketch, "E218", {"start": v(-50, 7400) * mm, "end": v(-810, 7400) * mm});
            skLineSegment(sketch, "E219", {"start": v(5870, 6220) * mm, "end": v(5870, 6820) * mm});
            skLineSegment(sketch, "E220", {"start": v(5870, 7010) * mm, "end": v(5870, 7770) * mm});
            skArc(sketch, "E221.trimOffspring", {"start": v(6407.4, 7547.4) * mm, "mid": v(6160.84, 7712.15) * mm, "end": v(5870, 7770) * mm});
            skLineSegment(sketch, "E222", {"start": v(3615, 6400) * mm, "end": v(3615, 5640) * mm});
            skLineSegment(sketch, "E223", {"start": v(3615, 7140) * mm, "end": v(3615, 7900) * mm});
            skLineSegment(sketch, "E224", {"start": v(5870, 9385) * mm, "end": v(5870, 10145) * mm});
            skLineSegment(sketch, "E225", {"start": v(4960, 10445) * mm, "end": v(4960, 10845) * mm});
            skArc(sketch, "E226", {"start": v(5384.26, 9969.26) * mm, "mid": v(5189.61, 10099.33) * mm, "end": v(4960, 10145) * mm});
            skLineSegment(sketch, "E227", {"start": v(4960, 9545) * mm, "end": v(4960, 10145) * mm});
            skLineSegment(sketch, "E228", {"start": v(4770, 13185) * mm, "end": v(4770, 12585) * mm});
            skLineSegment(sketch, "E229", {"start": v(4770, 11985) * mm, "end": v(4770, 12585) * mm});
            skLineSegment(sketch, "E230", {"start": v(5780, 10985) * mm, "end": v(5780, 11035) * mm});
            skLineSegment(sketch, "E231", {"start": v(5780, 11035) * mm, "end": v(4180, 11035) * mm});
            skLineSegment(sketch, "E232", {"start": v(4180, 11035) * mm, "end": v(4180, 10985) * mm});
            skLineSegment(sketch, "E233", {"start": v(4180, 10985) * mm, "end": v(5780, 10985) * mm});
            skLineSegment(sketch, "E234.bottom", {"start": v(-1720, 2970) * mm, "end": v(-100, 2970) * mm});
            skLineSegment(sketch, "E234.top", {"start": v(-1720, 3170) * mm, "end": v(-100, 3170) * mm});
            skLineSegment(sketch, "E234.left", {"start": v(-1720, 2970) * mm, "end": v(-1720, 3170) * mm});
            skLineSegment(sketch, "E234.right", {"start": v(-100, 2970) * mm, "end": v(-100, 3170) * mm});
            skLineSegment(sketch, "E235", {"start": v(4140, 10545) * mm, "end": v(4870, 10545) * mm, "construction": true});
            skCircle(sketch, "E236", {"center": v(4505, 10545) * mm, "radius": 250 * mm});
            skLineSegment(sketch, "E237", {"start": v(5600, 4105) * mm, "end": v(6137.4, 4642.4) * mm});
            skLineSegment(sketch, "E238", {"start": v(5600, 4105) * mm, "end": v(6360, 4105) * mm});
            skArc(sketch, "E239.trimOffspring", {"start": v(6360, 4105) * mm, "mid": v(6302.15, 4395.84) * mm, "end": v(6137.4, 4642.4) * mm});
            skLineSegment(sketch, "E240", {"start": v(6510, 5805) * mm, "end": v(7410, 5805) * mm});
            skLineSegment(sketch, "E241", {"start": v(7410, 5805) * mm, "end": v(7410, 5355) * mm});
            skLineSegment(sketch, "E242", {"start": v(7410, 5355) * mm, "end": v(6960, 4905) * mm});
            skLineSegment(sketch, "E243", {"start": v(6960, 4905) * mm, "end": v(6510, 4905) * mm});
            skLineSegment(sketch, "E244", {"start": v(6510, 4905) * mm, "end": v(6510, 5805) * mm});
            skLineSegment(sketch, "E245.bottom", {"start": v(6510, 4805) * mm, "end": v(6960, 4805) * mm});
            skLineSegment(sketch, "E245.top", {"start": v(6510, 4205) * mm, "end": v(6960, 4205) * mm});
            skLineSegment(sketch, "E245.left", {"start": v(6510, 4805) * mm, "end": v(6510, 4205) * mm});
            skLineSegment(sketch, "E245.right", {"start": v(6960, 4805) * mm, "end": v(6960, 4205) * mm});
            skCircle(sketch, "E246", {"center": v(6760, 5555) * mm, "radius": 40 * mm});
            skCircle(sketch, "E247", {"center": v(6710, 4505) * mm, "radius": 30 * mm});
            skLineSegment(sketch, "E248.bottom", {"start": v(7860, 5805) * mm, "end": v(8260, 5805) * mm});
            skLineSegment(sketch, "E248.top", {"start": v(7860, 5605) * mm, "end": v(7965.72, 5605) * mm});
            skLineSegment(sketch, "E248.left", {"start": v(7860, 5805) * mm, "end": v(7860, 5605) * mm});
            skLineSegment(sketch, "E248.right", {"start": v(8260, 5805) * mm, "end": v(8260, 5605) * mm});
            skLineSegment(sketch, "E249", {"start": v(8060, 5605) * mm, "end": v(8060, 5430) * mm, "construction": true});
            skLineSegment(sketch, "E250", {"start": v(8060, 5605) * mm, "end": v(8060, 5655) * mm, "construction": true});
            skEllipticalArc(sketch, "E251", {});
            skLineSegment(sketch, "E252", {"start": v(8060, 5430) * mm, "end": v(8060, 5205) * mm, "construction": true});
            skLineSegment(sketch, "E253", {"start": v(8060, 5430) * mm, "end": v(8210, 5430) * mm, "construction": true});
            skLineSegment(sketch, "E254.trimOffspring", {"start": v(8154.28, 5605) * mm, "end": v(8260, 5605) * mm});
            skPoint(sketch, "E255", {"position": v(6510, 4505) * mm});
            skLineSegment(sketch, "E256", {"start": v(6510, 5555) * mm, "end": v(6760, 5555) * mm, "construction": true});
            skLineSegment(sketch, "E257", {"start": v(6760, 5555) * mm, "end": v(6760, 5805) * mm, "construction": true});
            skLineSegment(sketch, "E258", {"start": v(6710, 4505) * mm, "end": v(6510, 4505) * mm, "construction": true});
            skLineSegment(sketch, "E259", {"start": v(8410, 4105.1) * mm, "end": v(7872.6, 4642.5) * mm});
            skArc(sketch, "E260", {"start": v(7872.6, 4642.5) * mm, "mid": v(7707.85, 4395.94) * mm, "end": v(7650, 4105.1) * mm});
            skLineSegment(sketch, "E261", {"start": v(8410, 4105.1) * mm, "end": v(7650, 4105.1) * mm});
            const initialGuessF16  = {"E251": [8.06, 5.43, 0, 1, 0.225, 0.15, 0.679673818908253, 5.603511488271334]};
            skSetInitialGuess(sketch, initialGuessF16);
            skSolve(sketch);
        }
        {
            var Q0;
            Q0 = qSketchRegion(id + "F16", true);
            extrude(context, id + "F17", {"entities" : qUnion([Q0]), "operationType" : NewBodyOperationType.ADD, "depth" : 0.5 * mm});
        }
        {
            var Q0;
            Q0=makeQuery(id+"F5.boolean.opBoolean","MERGE",FACE,{"derivedFrom":[makeQuery(id+"F1.opExtrude","SWEPT_FACE",FACE,{"disambiguationData":[OSD([sQuery(id+"F0.wireOp",EDGE,"E16"),sQuery(id+"F0.wireOp",EDGE,"E42")])]}),makeQuery(id+"F5.opExtrude","SWEPT_FACE",FACE,{"disambiguationData":[OSD([sQuery(id+"F4.wireOp",EDGE,"E82")])]})]});
            var sketch = newSketch(context, id + "F18", { "sketchPlane" : qUnion([Q0])});
            skLineSegment(sketch, "E262.bottom", {"start": v(435, 1775) * mm, "end": v(1635, 1775) * mm});
            skLineSegment(sketch, "E262.top", {"start": v(435, 1075) * mm, "end": v(1635, 1075) * mm});
            skLineSegment(sketch, "E262.left", {"start": v(435, 1775) * mm, "end": v(435, 1075) * mm});
            skLineSegment(sketch, "E262.right", {"start": v(1635, 1775) * mm, "end": v(1635, 1075) * mm});
            skLineSegment(sketch, "E263.bottom", {"start": v(-1945, 1975) * mm, "end": v(-165, 1975) * mm});
            skLineSegment(sketch, "E263.top", {"start": v(-1945, -25) * mm, "end": v(-165, -25) * mm});
            skLineSegment(sketch, "E263.left", {"start": v(-1945, 1975) * mm, "end": v(-1945, -25) * mm});
            skLineSegment(sketch, "E263.right", {"start": v(-165, 1975) * mm, "end": v(-165, -25) * mm});
            skLineSegment(sketch, "E264.bottom", {"start": v(-3745, 1975) * mm, "end": v(-2545, 1975) * mm});
            skLineSegment(sketch, "E264.top", {"start": v(-3745, 1075) * mm, "end": v(-2545, 1075) * mm});
            skLineSegment(sketch, "E264.left", {"start": v(-3745, 1975) * mm, "end": v(-3745, 1075) * mm});
            skLineSegment(sketch, "E264.right", {"start": v(-2545, 1975) * mm, "end": v(-2545, 1075) * mm});
            skSolve(sketch);
        }
        {
            var Q0;
            Q0 = qSketchRegion(id + "F18", true);
            extrude(context, id + "F19", {"entities" : qUnion([Q0]), "operationType" : NewBodyOperationType.ADD, "depth" : 0.5 * mm});
        }
        {
            var Q0;
            Q0=makeQuery(id+"F5.boolean.opBoolean","MERGE",FACE,{"derivedFrom":[makeQuery(id+"F1.opExtrude","SWEPT_FACE",FACE,{"disambiguationData":[OSD([sQuery(id+"F0.wireOp",EDGE,"E17")])]}),makeQuery(id+"F5.opExtrude","SWEPT_FACE",FACE,{"disambiguationData":[OSD([sQuery(id+"F4.wireOp",EDGE,"E81")])]})]});
            var sketch = newSketch(context, id + "F20", { "sketchPlane" : qUnion([Q0])});
            skLineSegment(sketch, "E265.bottom", {"start": v(-11735, 2175) * mm, "end": v(-11135, 2175) * mm});
            skLineSegment(sketch, "E265.top", {"start": v(-11735, 1575) * mm, "end": v(-11135, 1575) * mm});
            skLineSegment(sketch, "E265.left", {"start": v(-11735, 2175) * mm, "end": v(-11735, 1575) * mm});
            skLineSegment(sketch, "E265.right", {"start": v(-11135, 2175) * mm, "end": v(-11135, 1575) * mm});
            skSolve(sketch);
        }
        {
            var Q0;
            Q0 = qSketchRegion(id + "F20", true);
            extrude(context, id + "F21", {"entities" : qUnion([Q0]), "operationType" : NewBodyOperationType.ADD, "depth" : .25 * mm});
        }
        {
            var Q0;
            Q0=makeQuery(id+"F5.boolean.opBoolean","MERGE",FACE,{"derivedFrom":[makeQuery(id+"F1.opExtrude","SWEPT_FACE",FACE,{"disambiguationData":[OSD([sQuery(id+"F0.wireOp",EDGE,"E54")])]}),makeQuery(id+"F5.opExtrude","SWEPT_FACE",FACE,{"disambiguationData":[OSD([sQuery(id+"F4.wireOp",EDGE,"E84")])]})]});
            var sketch = newSketch(context, id + "F22", { "sketchPlane" : qUnion([Q0])});
            skLineSegment(sketch, "E266.bottom", {"start": v(-1680, -25) * mm, "end": v(-100, -25) * mm});
            skLineSegment(sketch, "E266.top", {"start": v(-1680, 1875) * mm, "end": v(-100, 1875) * mm});
            skLineSegment(sketch, "E266.left", {"start": v(-1680, -25) * mm, "end": v(-1680, 1875) * mm});
            skLineSegment(sketch, "E266.right", {"start": v(-100, -25) * mm, "end": v(-100, 1875) * mm});
            skSolve(sketch);
        }
        {
            var Q0;
            Q0 = qSketchRegion(id + "F22", true);
            extrude(context, id + "F23", {"entities" : qUnion([Q0]), "operationType" : NewBodyOperationType.ADD, "depth" : .25 * mm});
        }
        {
            var Q0;
            Q0=makeQuery(id+"F5.boolean.opBoolean","MERGE",FACE,{"derivedFrom":[makeQuery(id+"F1.opExtrude","SWEPT_FACE",FACE,{"disambiguationData":[OSD([sQuery(id+"F0.wireOp",EDGE,"E18")])]}),makeQuery(id+"F5.opExtrude","SWEPT_FACE",FACE,{"disambiguationData":[OSD([sQuery(id+"F4.wireOp",EDGE,"E80")])]})]});
            var sketch = newSketch(context, id + "F24", { "sketchPlane" : qUnion([Q0])});
            skLineSegment(sketch, "E267.bottom", {"start": v(-7525, 1975) * mm, "end": v(-5825, 1975) * mm});
            skLineSegment(sketch, "E267.top", {"start": v(-7525, 675) * mm, "end": v(-5825, 675) * mm});
            skLineSegment(sketch, "E267.left", {"start": v(-7525, 1975) * mm, "end": v(-7525, 675) * mm});
            skLineSegment(sketch, "E267.right", {"start": v(-5825, 1975) * mm, "end": v(-5825, 675) * mm});
            skSolve(sketch);
        }
        {
            var Q0;
            Q0 = qSketchRegion(id + "F24", true);
            extrude(context, id + "F25", {"entities" : qUnion([Q0]), "operationType" : NewBodyOperationType.ADD, "depth" : .25 * mm});
        }
        {
            var Q0;
            Q0=makeQuery(id+"F5.boolean.opBoolean","MERGE",FACE,{"derivedFrom":[makeQuery(id+"F1.opExtrude","SWEPT_FACE",FACE,{"disambiguationData":[OSD([sQuery(id+"F0.wireOp",EDGE,"E0.left")])]}),makeQuery(id+"F5.opExtrude","SWEPT_FACE",FACE,{"disambiguationData":[OSD([sQuery(id+"F4.wireOp",EDGE,"E85")])]})]});
            var sketch = newSketch(context, id + "F26", { "sketchPlane" : qUnion([Q0])});
            skLineSegment(sketch, "E268.bottom", {"start": v(-2600, 1975) * mm, "end": v(-900, 1975) * mm});
            skLineSegment(sketch, "E268.top", {"start": v(-2600, 675) * mm, "end": v(-900, 675) * mm});
            skLineSegment(sketch, "E268.left", {"start": v(-2600, 1975) * mm, "end": v(-2600, 675) * mm});
            skLineSegment(sketch, "E268.right", {"start": v(-900, 1975) * mm, "end": v(-900, 675) * mm});
            skSolve(sketch);
        }
        {
            var Q0;
            Q0 = qSketchRegion(id + "F26", true);
            extrude(context, id + "F27", {"entities" : qUnion([Q0]), "operationType" : NewBodyOperationType.ADD, "depth" : 0.25 * mm});
        }
        {
            var Q0;
            Q0=makeQuery(id+"F5.boolean.opBoolean","MERGE",FACE,{"derivedFrom":[makeQuery(id+"F1.opExtrude","SWEPT_FACE",FACE,{"disambiguationData":[OSD([sQuery(id+"F0.wireOp",EDGE,"E43"),sQuery(id+"F0.wireOp",EDGE,"E53")])]}),makeQuery(id+"F5.opExtrude","SWEPT_FACE",FACE,{"disambiguationData":[OSD([sQuery(id+"F4.wireOp",EDGE,"E83")])]})]});
            var sketch = newSketch(context, id + "F28", { "sketchPlane" : qUnion([Q0])});
            skLineSegment(sketch, "E269.bottom", {"start": v(-6093.89, 1975) * mm, "end": v(-4793.89, 1975) * mm});
            skLineSegment(sketch, "E269.top", {"start": v(-6093.89, 1175) * mm, "end": v(-4793.89, 1175) * mm});
            skLineSegment(sketch, "E269.left", {"start": v(-6093.89, 1975) * mm, "end": v(-6093.89, 1175) * mm});
            skLineSegment(sketch, "E269.right", {"start": v(-4793.89, 1975) * mm, "end": v(-4793.89, 1175) * mm});
            skLineSegment(sketch, "E270", {"start": v(-7293.89, -25) * mm, "end": v(-7293.89, 2005) * mm, "construction": true});
            skSolve(sketch);
        }
        {
            var Q0;
            Q0 = qSketchRegion(id + "F28", true);
            extrude(context, id + "F29", {"entities" : qUnion([Q0]), "operationType" : NewBodyOperationType.ADD, "depth" : 0.05 * mm});
        }
        {
            var Q0;
            Q0=makeQuery(id+"F5.boolean.opBoolean","MERGE",FACE,{"derivedFrom":[makeQuery(id+"F1.opExtrude","SWEPT_FACE",FACE,{"disambiguationData":[OSD([sQuery(id+"F0.wireOp",EDGE,"E43"),sQuery(id+"F0.wireOp",EDGE,"E53")])]}),makeQuery(id+"F5.opExtrude","SWEPT_FACE",FACE,{"disambiguationData":[OSD([sQuery(id+"F4.wireOp",EDGE,"E83")])]})]});
            var sketch = newSketch(context, id + "F30", { "sketchPlane" : qUnion([Q0])});
            skLineSegment(sketch, "E271.bottom", {"start": v(-9335, -25) * mm, "end": v(-6293.89, -25) * mm});
            skLineSegment(sketch, "E271.top", {"start": v(-9335, 2005) * mm, "end": v(-6293.89, 2005) * mm});
            skLineSegment(sketch, "E271.left", {"start": v(-9335, -25) * mm, "end": v(-9335, 2005) * mm});
            skLineSegment(sketch, "E271.right", {"start": v(-6293.89, -25) * mm, "end": v(-6293.89, 2005) * mm});
            skSolve(sketch);
        }
        {
            var Q0;
            Q0 = qSketchRegion(id + "F30", true);
            extrude(context, id + "F31", {"entities" : qUnion([Q0]), "operationType" : NewBodyOperationType.ADD, "depth" : 0.05 * mm});
        }
        {
            var Q0;
            Q0=makeQuery(id+"F23.opExtrude","CAP_FACE",FACE,{"disambiguationData":[OSD([sQuery(id+"F22.wireOp",EDGE,"E266.bottom"),sQuery(id+"F22.wireOp",EDGE,"E266.top"),sQuery(id+"F22.wireOp",EDGE,"E266.left"),sQuery(id+"F22.wireOp",EDGE,"E266.right")])],"isStart":false});
            var sketch = newSketch(context, id + "F32", { "sketchPlane" : qUnion([Q0])});
            skLineSegment(sketch, "E272.bottom", {"start": v(-100, 1875) * mm, "end": v(-900, 1875) * mm});
            skLineSegment(sketch, "E272.top", {"start": v(-100, 175) * mm, "end": v(-900, 175) * mm});
            skLineSegment(sketch, "E272.left", {"start": v(-100, 1875) * mm, "end": v(-100, 175) * mm});
            skLineSegment(sketch, "E272.right", {"start": v(-900, 1875) * mm, "end": v(-900, 175) * mm});
            skSolve(sketch);
        }
        {
            var Q0;
            Q0 = qSketchRegion(id + "F32", true);
            extrude(context, id + "F33", {"entities" : qUnion([Q0]), "operationType" : NewBodyOperationType.ADD, "depth" : 0.25 * mm});
        }
    });
